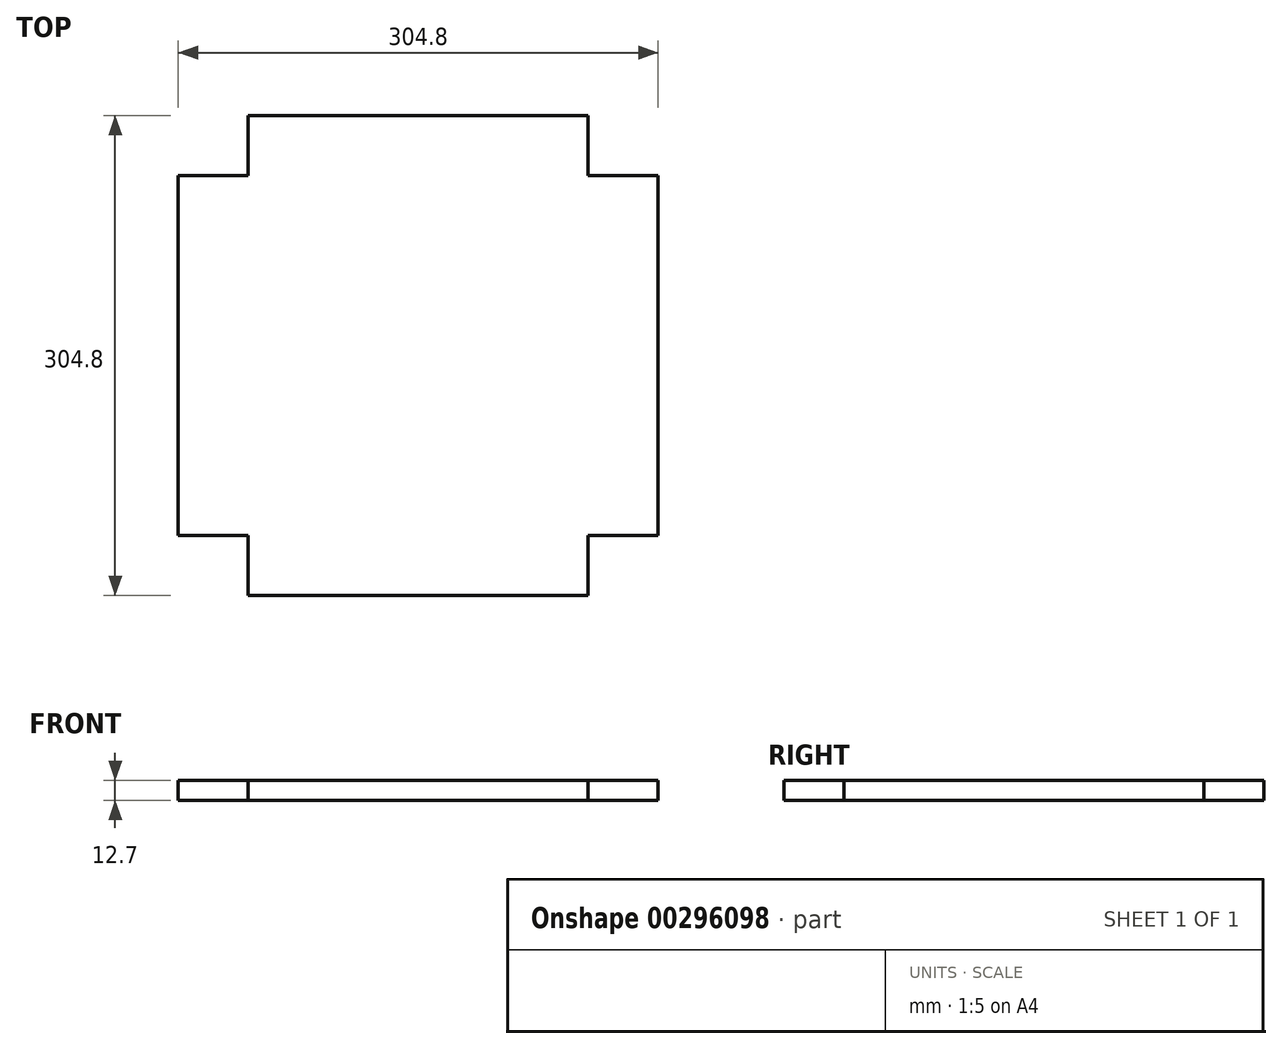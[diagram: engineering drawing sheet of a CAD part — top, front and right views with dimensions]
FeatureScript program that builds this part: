
annotation { "Feature Type Name" : "Feature", "Feature Type Description" : "" }
export const myFeature = defineFeature(function(context is Context, id is Id, definition is map)
    precondition{}
    {
        {
            var Q0;
            Q0=qCreatedBy(makeId("Top.planeOp"),FACE);
            var sketch = newSketch(context, id + "F0", { "sketchPlane" : qUnion([Q0])});
            skLineSegment(sketch, "E0", {"start": v(-104.24, 182.97) * mm, "end": v(111.66, 182.97) * mm});
            skLineSegment(sketch, "E1", {"start": v(111.66, 182.97) * mm, "end": v(111.66, 144.87) * mm});
            skLineSegment(sketch, "E2", {"start": v(111.66, 144.87) * mm, "end": v(156.1, 144.87) * mm});
            skLineSegment(sketch, "E3", {"start": v(156.1, 144.87) * mm, "end": v(156.1, -83.73) * mm});
            skLineSegment(sketch, "E4", {"start": v(156.1, -83.73) * mm, "end": v(111.66, -83.73) * mm});
            skLineSegment(sketch, "E5", {"start": v(111.66, -83.73) * mm, "end": v(111.66, -121.83) * mm});
            skLineSegment(sketch, "E6", {"start": v(111.66, -121.83) * mm, "end": v(-104.24, -121.83) * mm});
            skLineSegment(sketch, "E7", {"start": v(-104.24, -121.83) * mm, "end": v(-104.24, -83.73) * mm});
            skLineSegment(sketch, "E8", {"start": v(-104.24, -83.73) * mm, "end": v(-148.7, -83.73) * mm});
            skLineSegment(sketch, "E9", {"start": v(-148.7, -83.73) * mm, "end": v(-148.7, 144.87) * mm});
            skLineSegment(sketch, "E10", {"start": v(-148.7, 144.87) * mm, "end": v(-104.24, 144.87) * mm});
            skLineSegment(sketch, "E11", {"start": v(-104.24, 144.87) * mm, "end": v(-104.24, 182.97) * mm});
            skSolve(sketch);
        }
        {
            var Q0;
            Q0=makeQuery(id+"F0.imprint","IMPRINT",FACE,{"disambiguationData":[TD([[makeQuery(id+"F0.imprint","IMPRINT",EDGE,{"derivedFrom":sQuery(id+"F0.wireOp",EDGE,"E0")}),-1.0]])]});
            extrude(context, id + "F1", {"entities" : qUnion([Q0]), "depth" : 12.7 * mm});
        }
    });
